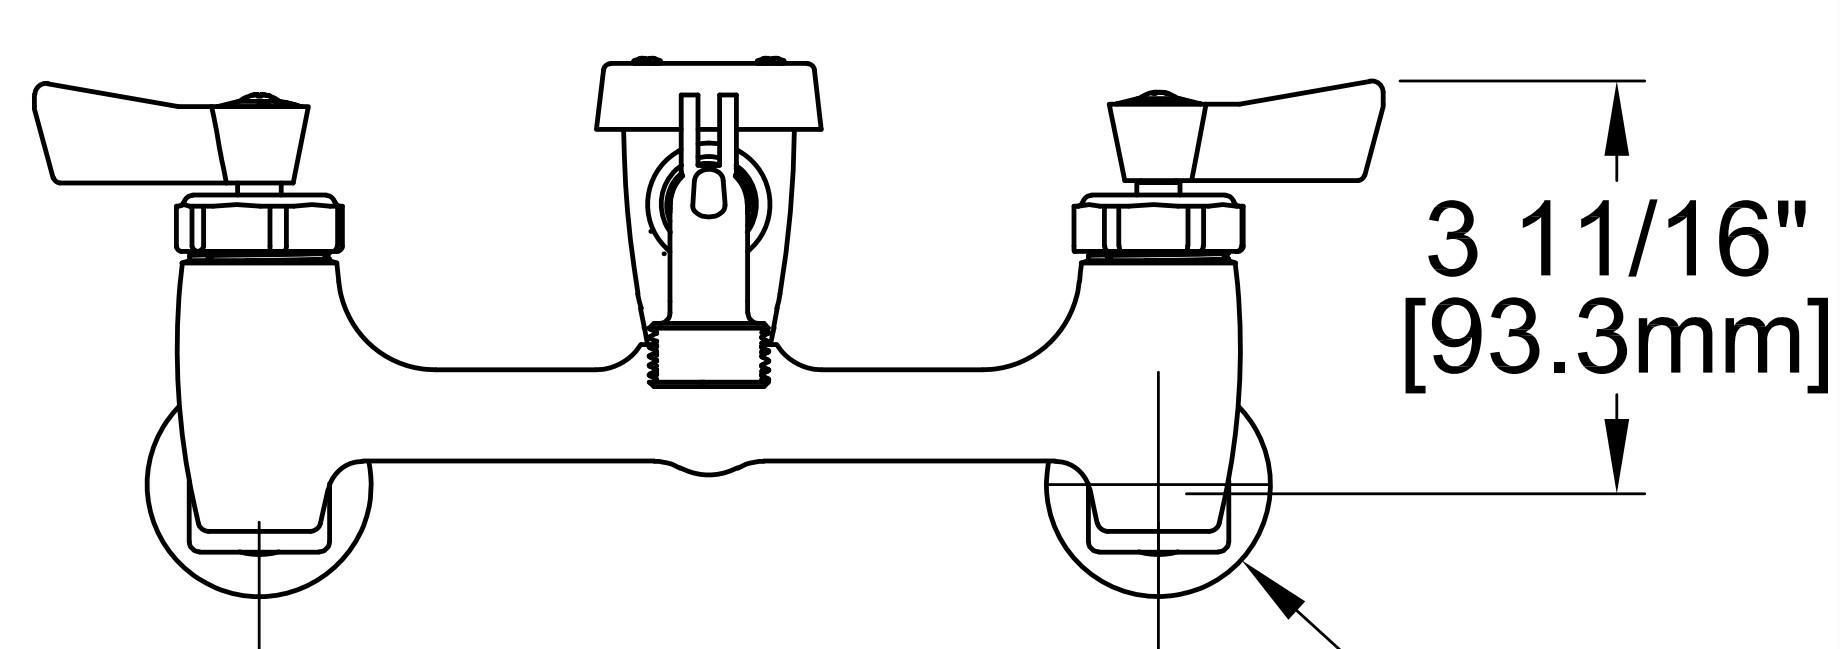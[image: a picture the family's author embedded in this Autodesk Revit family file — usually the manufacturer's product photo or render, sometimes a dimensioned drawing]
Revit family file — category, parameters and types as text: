
# Revit family: FACB-KF-CRL_47500
name_source: partatom
category: Plumbing Fixtures
units: mm (PartAtom-declared; Revit-internal decimal feet)

## family parameters
Always vertical = Yes
Cut with Voids When Loaded = No
OmniClass Number = 23.45.00.00
OmniClass Title = Sanitary, Laundry, and Cleaning Equipment
Part Type = Normal
Room Calculation Point = No
Round Connector Dimension = Use Diameter
Shared = No
Work Plane-Based = No

## types (1)
- FACB-KF-CRL_47500
    Cold Water Consumption = 0 GPM
    Cold Water Flow = 2 GPM
    Cold Water Maximum Pressure = 200.00 psi
    Cold Water Minimum Pressure = 80.00 psi
    Cold Water Size = 1/2"
    Cold Water Temperature Recommended = 40 °F
    Fixture Height = 4' - 0"
    Hot Cold Inlet Spacing = 8"
    Hot Water Consumption = 0 GPM
    Hot Water Flow = 2 GPM
    Hot Water Maximum Pressure = 200.00 psi
    Hot Water Minimum Pressure = 80.00 psi
    Hot Water Size = 1/2"
    Hot Water Temperature = 40 °F

## geometry (parser evidence)
native form markers: Sweep x20
no freeform markers — native parametric forms only
